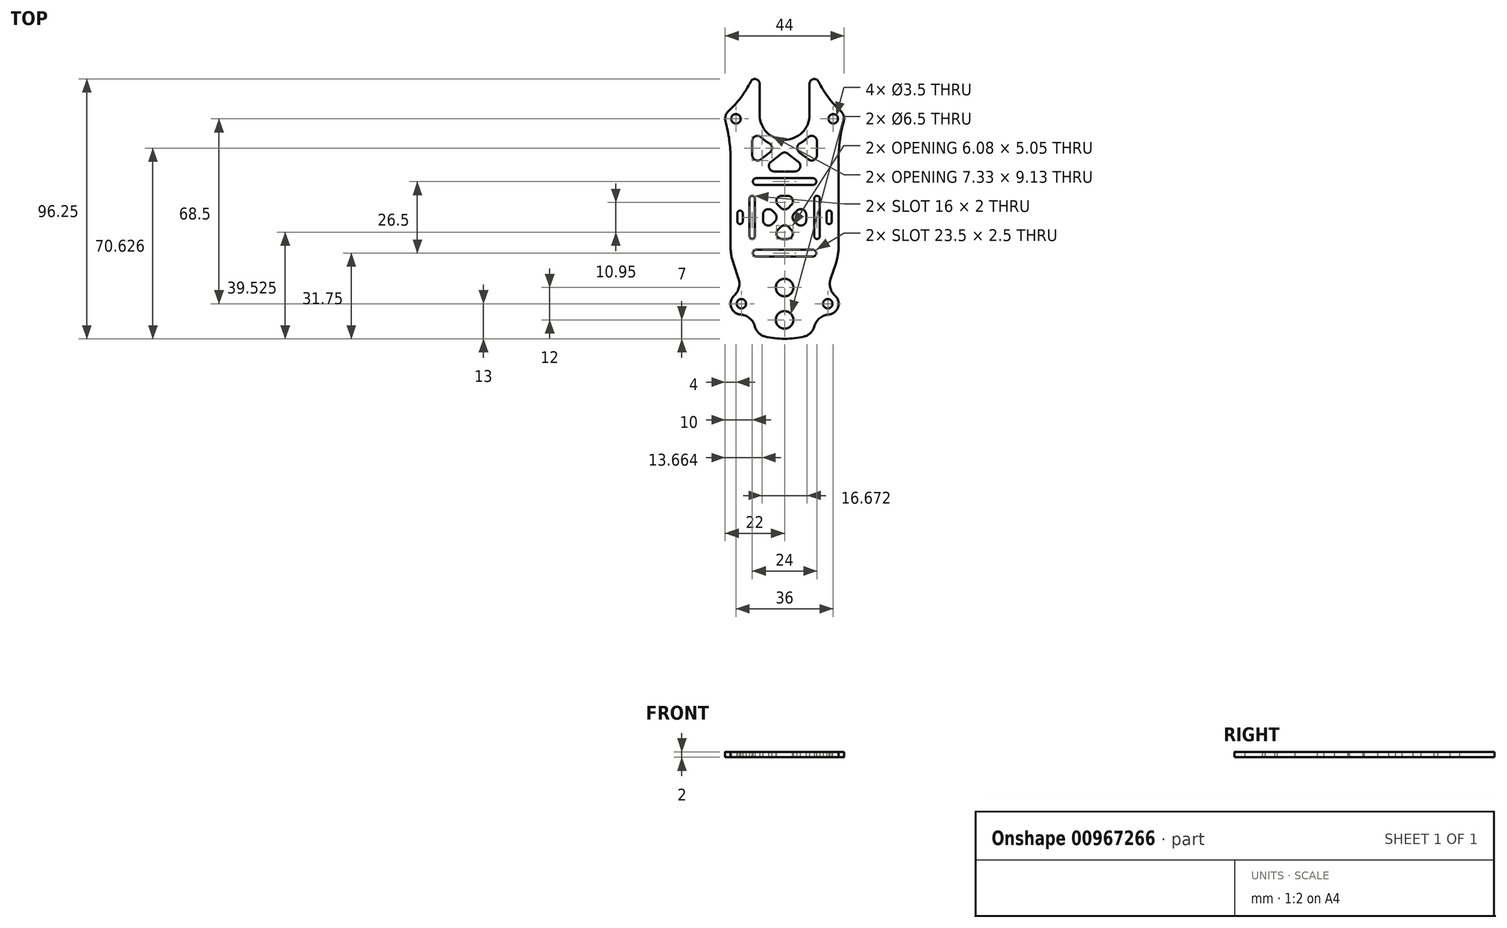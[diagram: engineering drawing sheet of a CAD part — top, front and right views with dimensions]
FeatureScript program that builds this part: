
annotation { "Feature Type Name" : "Feature", "Feature Type Description" : "" }
export const myFeature = defineFeature(function(context is Context, id is Id, definition is map)
    precondition{}
    {
        {
            var Q0;
            Q0=qCreatedBy(makeId("Top.planeOp"),FACE);
            var sketch = newSketch(context, id + "F0", { "sketchPlane" : qUnion([Q0])});
            skArc(sketch, "E0", {"start": v(-20.7, 39.46) * mm, "mid": v(-21.84, 37.62) * mm, "end": v(-21.86, 35.44) * mm});
            skLineSegment(sketch, "E1", {"start": v(-18.93, -17.14) * mm, "end": v(-17.05, -22.66) * mm});
            skLineSegment(sketch, "E2", {"start": v(0, 24) * mm, "end": v(0, -60) * mm, "construction": true});
            skCircle(sketch, "E3", {"center": v(-16, -32) * mm, "radius": 1.75 * mm});
            skArc(sketch, "E4.MirrorCS", {"start": v(20.7, 39.46) * mm, "mid": v(21.84, 37.62) * mm, "end": v(21.86, 35.44) * mm});
            skCircle(sketch, "E5.MirrorC", {"center": v(16, -32) * mm, "radius": 1.75 * mm});
            skLineSegment(sketch, "E6.MirrorCS", {"start": v(18.93, -17.14) * mm, "end": v(17.05, -22.66) * mm});
            skCircle(sketch, "E7", {"center": v(-18, 36.5) * mm, "radius": 1.75 * mm});
            skCircle(sketch, "E8.MirrorC", {"center": v(18, 36.5) * mm, "radius": 1.75 * mm});
            skCircle(sketch, "E9", {"center": v(0, -38) * mm, "radius": 3.25 * mm});
            skArc(sketch, "E10", {"start": v(-7.28, -44.13) * mm, "mid": v(-3.66, -44.78) * mm, "end": v(0, -45) * mm});
            skLineSegment(sketch, "E11.trimOffspring", {"start": v(-20, 21.67) * mm, "end": v(-20, -10.69) * mm});
            skArc(sketch, "E12", {"start": v(16.32, -35.99) * mm, "mid": v(19.79, -33.3) * mm, "end": v(18.7, -29.04) * mm});
            skArc(sketch, "E13.filletArc", {"start": v(16.32, -35.99) * mm, "mid": v(13.12, -37.23) * mm, "end": v(11.13, -40.03) * mm});
            skArc(sketch, "E14.filletArc", {"start": v(17.05, -22.66) * mm, "mid": v(16.92, -26.1) * mm, "end": v(18.7, -29.04) * mm});
            skArc(sketch, "E15.MirrorCS", {"start": v(-16.32, -35.99) * mm, "mid": v(-13.12, -37.23) * mm, "end": v(-11.13, -40.03) * mm});
            skArc(sketch, "E16.MirrorCS", {"start": v(-16.32, -35.99) * mm, "mid": v(-19.79, -33.3) * mm, "end": v(-18.7, -29.04) * mm});
            skArc(sketch, "E17.MirrorCS", {"start": v(-17.05, -22.66) * mm, "mid": v(-16.92, -26.1) * mm, "end": v(-18.7, -29.04) * mm});
            skLineSegment(sketch, "E18", {"start": v(-11.13, -40.03) * mm, "end": v(-10.84, -40.89) * mm});
            skLineSegment(sketch, "E19", {"start": v(11.13, -40.03) * mm, "end": v(10.84, -40.89) * mm});
            skLineSegment(sketch, "E20", {"start": v(-17.05, -22.66) * mm, "end": v(-11.13, -40.03) * mm, "construction": true});
            skLineSegment(sketch, "E21", {"start": v(17.05, -22.66) * mm, "end": v(11.13, -40.03) * mm, "construction": true});
            skArc(sketch, "E22", {"start": v(-9.25, 49.5) * mm, "mid": v(-10.6, 51.2) * mm, "end": v(-12.57, 50.27) * mm});
            skArc(sketch, "E23", {"start": v(-20.7, 39.46) * mm, "mid": v(-16.12, 44.48) * mm, "end": v(-12.57, 50.27) * mm});
            skArc(sketch, "E24.MirrorCS", {"start": v(9.25, 49.5) * mm, "mid": v(10.6, 51.2) * mm, "end": v(12.57, 50.27) * mm});
            skArc(sketch, "E25.MirrorCS", {"start": v(20.7, 39.46) * mm, "mid": v(16.12, 44.48) * mm, "end": v(12.57, 50.27) * mm});
            skPoint(sketch, "E26.visualSharp", {"position": v(-10, -43.34) * mm});
            skArc(sketch, "E26.filletArc", {"start": v(-10.84, -40.89) * mm, "mid": v(-9.47, -42.97) * mm, "end": v(-7.28, -44.13) * mm});
            skPoint(sketch, "E27.visualSharp", {"position": v(10, -43.34) * mm});
            skArc(sketch, "E27.filletArc", {"start": v(7.28, -44.13) * mm, "mid": v(9.47, -42.97) * mm, "end": v(10.84, -40.89) * mm});
            skLineSegment(sketch, "E28", {"start": v(-16.5, 1.5) * mm, "end": v(-16.5, -1.5) * mm, "construction": true});
            skArc(sketch, "E29.0.startCap", {"start": v(-17.5, 1.5) * mm, "mid": v(-16.5, 2.5) * mm, "end": v(-15.5, 1.5) * mm});
            skArc(sketch, "E29.0.endCap", {"start": v(-15.5, -1.5) * mm, "mid": v(-16.5, -2.5) * mm, "end": v(-17.5, -1.5) * mm});
            skLineSegment(sketch, "E29.0.left", {"start": v(-15.5, 1.5) * mm, "end": v(-15.5, -1.5) * mm});
            skLineSegment(sketch, "E29.0.right", {"start": v(-17.5, 1.5) * mm, "end": v(-17.5, -1.5) * mm});
            skLineSegment(sketch, "E30.MirrorCS", {"start": v(16.5, 1.5) * mm, "end": v(16.5, -1.5) * mm, "construction": true});
            skLineSegment(sketch, "E31.MirrorCS", {"start": v(15.5, 1.5) * mm, "end": v(15.5, -1.5) * mm});
            skLineSegment(sketch, "E32.MirrorCS", {"start": v(17.5, 1.5) * mm, "end": v(17.5, -1.5) * mm});
            skArc(sketch, "E33.MirrorCS", {"start": v(17.5, 1.5) * mm, "mid": v(16.5, 2.5) * mm, "end": v(15.5, 1.5) * mm});
            skArc(sketch, "E34.MirrorCS", {"start": v(15.5, -1.5) * mm, "mid": v(16.5, -2.5) * mm, "end": v(17.5, -1.5) * mm});
            skArc(sketch, "E35", {"start": v(-20, 21.67) * mm, "mid": v(-20.47, 28.62) * mm, "end": v(-21.86, 35.44) * mm});
            skArc(sketch, "E36.MirrorCS", {"start": v(20, 21.67) * mm, "mid": v(20.47, 28.62) * mm, "end": v(21.86, 35.44) * mm});
            skCircle(sketch, "E37", {"center": v(0, -38) * mm, "radius": 4.5 * mm, "construction": true});
            skLineSegment(sketch, "E38", {"start": v(20, 21.67) * mm, "end": v(20, -10.69) * mm});
            skLineSegment(sketch, "E39", {"start": v(-10.5, 13.25) * mm, "end": v(10.5, 13.25) * mm, "construction": true});
            skLineSegment(sketch, "E40", {"start": v(-10.5, -13.25) * mm, "end": v(10.5, -13.25) * mm, "construction": true});
            skArc(sketch, "E41.0.startCap", {"start": v(-10.5, 12) * mm, "mid": v(-11.75, 13.25) * mm, "end": v(-10.5, 14.5) * mm});
            skArc(sketch, "E41.0.endCap", {"start": v(10.5, 14.5) * mm, "mid": v(11.75, 13.25) * mm, "end": v(10.5, 12) * mm});
            skLineSegment(sketch, "E41.0.left", {"start": v(-10.5, 14.5) * mm, "end": v(10.5, 14.5) * mm});
            skLineSegment(sketch, "E41.0.right", {"start": v(-10.5, 12) * mm, "end": v(10.5, 12) * mm});
            skArc(sketch, "E41.1.startCap", {"start": v(-10.5, -14.5) * mm, "mid": v(-11.75, -13.25) * mm, "end": v(-10.5, -12) * mm});
            skArc(sketch, "E41.1.endCap", {"start": v(10.5, -12) * mm, "mid": v(11.75, -13.25) * mm, "end": v(10.5, -14.5) * mm});
            skLineSegment(sketch, "E41.1.left", {"start": v(-10.5, -12) * mm, "end": v(10.5, -12) * mm});
            skLineSegment(sketch, "E41.1.right", {"start": v(-10.5, -14.5) * mm, "end": v(10.5, -14.5) * mm});
            skPoint(sketch, "E42.visualSharp", {"position": v(-20, -14) * mm});
            skArc(sketch, "E42.filletArc", {"start": v(-20, -10.69) * mm, "mid": v(-19.73, -13.96) * mm, "end": v(-18.93, -17.14) * mm});
            skPoint(sketch, "E43.visualSharp", {"position": v(20, -14) * mm});
            skArc(sketch, "E43.filletArc", {"start": v(18.93, -17.14) * mm, "mid": v(19.73, -13.96) * mm, "end": v(20, -10.69) * mm});
            skLineSegment(sketch, "E44", {"start": v(-12, 7) * mm, "end": v(-12, -7) * mm, "construction": true});
            skLineSegment(sketch, "E45.MirrorCS", {"start": v(12, 7) * mm, "end": v(12, -7) * mm, "construction": true});
            skArc(sketch, "E46.0.startCap", {"start": v(-13, 7) * mm, "mid": v(-12, 8) * mm, "end": v(-11, 7) * mm});
            skArc(sketch, "E46.0.endCap", {"start": v(-11, -7) * mm, "mid": v(-12, -8) * mm, "end": v(-13, -7) * mm});
            skLineSegment(sketch, "E46.0.left", {"start": v(-11, 7) * mm, "end": v(-11, -7) * mm});
            skLineSegment(sketch, "E46.0.right", {"start": v(-13, 7) * mm, "end": v(-13, -7) * mm});
            skArc(sketch, "E46.3.startCap", {"start": v(11, 7) * mm, "mid": v(12, 8) * mm, "end": v(13, 7) * mm});
            skArc(sketch, "E46.3.endCap", {"start": v(13, -7) * mm, "mid": v(12, -8) * mm, "end": v(11, -7) * mm});
            skLineSegment(sketch, "E46.3.left", {"start": v(13, 7) * mm, "end": v(13, -7) * mm});
            skLineSegment(sketch, "E46.3.right", {"start": v(11, 7) * mm, "end": v(11, -7) * mm});
            skPoint(sketch, "E47.startSnap0", {"position": v(-16.5, 2.5) * mm});
            skArc(sketch, "E48.trimOffspring", {"start": v(0, -45) * mm, "mid": v(3.66, -44.78) * mm, "end": v(7.28, -44.13) * mm});
            skCircle(sketch, "E49", {"center": v(0, -26) * mm, "radius": 3.25 * mm});
            skLineSegment(sketch, "E50", {"start": v(-9.25, 49.5) * mm, "end": v(-9.25, 38) * mm});
            skLineSegment(sketch, "E51.MirrorCS", {"start": v(9.25, 49.5) * mm, "end": v(9.25, 38) * mm});
            skArc(sketch, "E52", {"start": v(-9.25, 38) * mm, "mid": v(0, 28.75) * mm, "end": v(9.25, 38) * mm});
            skSolve(sketch);
        }
        {
            var Q0;
            Q0=qSketchRegion(id+"F0",true);
            var Q1;
            Q1=makeQuery(id+"F0.imprint","IMPRINT",FACE,{"disambiguationData":[TD([[makeQuery(id+"F0.imprint","IMPRINT",EDGE,{"derivedFrom":sQuery(id+"F0.wireOp",EDGE,"f439a884-37bc-483a-9020-57d0572b4fa8.sketch_text.stroke-0")}),-1.0]])]});
            var Q2;
            Q2=makeQuery(id+"F0.imprint","IMPRINT",FACE,{"disambiguationData":[TD([[makeQuery(id+"F0.imprint","IMPRINT",EDGE,{"derivedFrom":sQuery(id+"F0.wireOp",EDGE,"f439a884-37bc-483a-9020-57d0572b4fa8.sketch_text.stroke-27")}),-1.0]])]});
            extrude(context, id + "F1", {"entities" : qUnion([Q0, Q1, Q2]), "depth" : 2 * mm});
        }
        {
            var Q0;
            Q0=makeQuery(id+"F1.opExtrude","CAP_FACE",FACE,{"disambiguationData":[OSD([sQuery(id+"F0.wireOp",EDGE,"E0"),sQuery(id+"F0.wireOp",EDGE,"E1"),sQuery(id+"F0.wireOp",EDGE,"E3"),sQuery(id+"F0.wireOp",EDGE,"E4.MirrorCS"),sQuery(id+"F0.wireOp",EDGE,"E5.MirrorC"),sQuery(id+"F0.wireOp",EDGE,"E6.MirrorCS"),sQuery(id+"F0.wireOp",EDGE,"E7"),sQuery(id+"F0.wireOp",EDGE,"E8.MirrorC"),sQuery(id+"F0.wireOp",EDGE,"E9"),sQuery(id+"F0.wireOp",EDGE,"E10"),sQuery(id+"F0.wireOp",EDGE,"E11.trimOffspring"),sQuery(id+"F0.wireOp",EDGE,"E12"),sQuery(id+"F0.wireOp",EDGE,"E13.filletArc"),sQuery(id+"F0.wireOp",EDGE,"E14.filletArc"),sQuery(id+"F0.wireOp",EDGE,"E15.MirrorCS"),sQuery(id+"F0.wireOp",EDGE,"E16.MirrorCS"),sQuery(id+"F0.wireOp",EDGE,"E17.MirrorCS"),sQuery(id+"F0.wireOp",EDGE,"E18"),sQuery(id+"F0.wireOp",EDGE,"E19"),sQuery(id+"F0.wireOp",EDGE,"E22"),sQuery(id+"F0.wireOp",EDGE,"E23"),sQuery(id+"F0.wireOp",EDGE,"E24.MirrorCS"),sQuery(id+"F0.wireOp",EDGE,"E25.MirrorCS"),sQuery(id+"F0.wireOp",EDGE,"E26.filletArc"),sQuery(id+"F0.wireOp",EDGE,"E27.filletArc"),sQuery(id+"F0.wireOp",EDGE,"E29.0.startCap"),sQuery(id+"F0.wireOp",EDGE,"E29.0.endCap"),sQuery(id+"F0.wireOp",EDGE,"E29.0.left"),sQuery(id+"F0.wireOp",EDGE,"E29.0.right"),sQuery(id+"F0.wireOp",EDGE,"E31.MirrorCS"),sQuery(id+"F0.wireOp",EDGE,"E32.MirrorCS"),sQuery(id+"F0.wireOp",EDGE,"E33.MirrorCS"),sQuery(id+"F0.wireOp",EDGE,"E34.MirrorCS"),sQuery(id+"F0.wireOp",EDGE,"E35"),sQuery(id+"F0.wireOp",EDGE,"E36.MirrorCS"),sQuery(id+"F0.wireOp",EDGE,"E38"),sQuery(id+"F0.wireOp",EDGE,"E41.0.startCap"),sQuery(id+"F0.wireOp",EDGE,"E41.0.endCap"),sQuery(id+"F0.wireOp",EDGE,"E41.0.left"),sQuery(id+"F0.wireOp",EDGE,"E41.0.right"),sQuery(id+"F0.wireOp",EDGE,"E41.1.startCap"),sQuery(id+"F0.wireOp",EDGE,"E41.1.endCap"),sQuery(id+"F0.wireOp",EDGE,"E41.1.left"),sQuery(id+"F0.wireOp",EDGE,"E41.1.right"),sQuery(id+"F0.wireOp",EDGE,"E42.filletArc"),sQuery(id+"F0.wireOp",EDGE,"E43.filletArc"),sQuery(id+"F0.wireOp",EDGE,"E46.0.startCap"),sQuery(id+"F0.wireOp",EDGE,"E46.0.endCap"),sQuery(id+"F0.wireOp",EDGE,"E46.0.left"),sQuery(id+"F0.wireOp",EDGE,"E46.0.right"),sQuery(id+"F0.wireOp",EDGE,"E46.3.startCap"),sQuery(id+"F0.wireOp",EDGE,"E46.3.endCap"),sQuery(id+"F0.wireOp",EDGE,"E46.3.left"),sQuery(id+"F0.wireOp",EDGE,"E46.3.right"),sQuery(id+"F0.wireOp",EDGE,"E48.trimOffspring"),sQuery(id+"F0.wireOp",EDGE,"E49"),sQuery(id+"F0.wireOp",EDGE,"E50"),sQuery(id+"F0.wireOp",EDGE,"E51.MirrorCS"),sQuery(id+"F0.wireOp",EDGE,"E52")])],"isStart":false});
            var sketch = newSketch(context, id + "F2", { "sketchPlane" : qUnion([Q0])});
            skLineSegment(sketch, "E53.bottom", {"start": v(-1.05, 8) * mm, "end": v(1.05, 8) * mm});
            skLineSegment(sketch, "E53.top", {"start": v(-1.05, -8) * mm, "end": v(1.05, -8) * mm});
            skLineSegment(sketch, "E53.left", {"start": v(-8, 1.05) * mm, "end": v(-8, -1.05) * mm});
            skLineSegment(sketch, "E53.right", {"start": v(8, 1.05) * mm, "end": v(8, -1.05) * mm});
            skLineSegment(sketch, "E54.bottom", {"start": v(-12, 36) * mm, "end": v(12, 36) * mm, "construction": true});
            skLineSegment(sketch, "E54.top", {"start": v(-3.83, 17) * mm, "end": v(3.83, 17) * mm});
            skLineSegment(sketch, "E54.left", {"start": v(-12, 28.2) * mm, "end": v(-12, 23.05) * mm});
            skLineSegment(sketch, "E54.right", {"start": v(12, 28.2) * mm, "end": v(12, 23.05) * mm});
            skArc(sketch, "E55", {"start": v(-8.57, 29.6) * mm, "mid": v(-7.22, 28.42) * mm, "end": v(-5.71, 27.45) * mm});
            skPoint(sketch, "E55.centerSnap0", {"position": v(0, 36) * mm});
            skLineSegment(sketch, "E56", {"start": v(-8, 8) * mm, "end": v(8, -8) * mm, "construction": true});
            skLineSegment(sketch, "E57", {"start": v(-8, -8) * mm, "end": v(8, 8) * mm, "construction": true});
            skLineSegment(sketch, "E58", {"start": v(-12, 36) * mm, "end": v(12, 17) * mm, "construction": true});
            skLineSegment(sketch, "E59", {"start": v(-12, 17) * mm, "end": v(12, 36) * mm, "construction": true});
            skLineSegment(sketch, "E60", {"start": v(1.24, 23.6) * mm, "end": v(5.08, 20.57) * mm});
            skLineSegment(sketch, "E61", {"start": v(5.42, 24.12) * mm, "end": v(8.76, 21.48) * mm});
            skLineSegment(sketch, "E62.MirrorCS", {"start": v(-5.42, 24.12) * mm, "end": v(-8.76, 21.48) * mm});
            skLineSegment(sketch, "E63.MirrorCS", {"start": v(-1.24, 23.6) * mm, "end": v(-5.08, 20.57) * mm});
            skArc(sketch, "E64.trimOffspring", {"start": v(5.71, 27.45) * mm, "mid": v(7.22, 28.42) * mm, "end": v(8.57, 29.6) * mm});
            skPoint(sketch, "E65.orphan", {"position": v(2, 26.17) * mm});
            skPoint(sketch, "E66.orphan", {"position": v(-2, 26.17) * mm});
            skLineSegment(sketch, "E67", {"start": v(-12, 38) * mm, "end": v(-12, 36) * mm, "construction": true});
            skLineSegment(sketch, "E68", {"start": v(12, 38) * mm, "end": v(12, 36) * mm, "construction": true});
            skPoint(sketch, "E69.visualSharp", {"position": v(-12, 38) * mm});
            skArc(sketch, "E69.filletArc", {"start": v(-8.57, 29.6) * mm, "mid": v(-10.76, 30.05) * mm, "end": v(-12, 28.2) * mm});
            skPoint(sketch, "E70.visualSharp", {"position": v(-2.67, 26.3) * mm});
            skArc(sketch, "E70.filletArc", {"start": v(-5.42, 24.12) * mm, "mid": v(-4.67, 25.86) * mm, "end": v(-5.71, 27.45) * mm});
            skPoint(sketch, "E71.visualSharp", {"position": v(-12, 18.91) * mm});
            skArc(sketch, "E71.filletArc", {"start": v(-12, 23.05) * mm, "mid": v(-10.87, 21.25) * mm, "end": v(-8.76, 21.48) * mm});
            skPoint(sketch, "E72.visualSharp", {"position": v(-9.58, 17) * mm});
            skArc(sketch, "E72.filletArc", {"start": v(-5.08, 20.57) * mm, "mid": v(-5.72, 18.34) * mm, "end": v(-3.83, 17) * mm});
            skPoint(sketch, "E73.visualSharp", {"position": v(9.58, 17) * mm});
            skArc(sketch, "E73.filletArc", {"start": v(3.83, 17) * mm, "mid": v(5.72, 18.34) * mm, "end": v(5.08, 20.57) * mm});
            skPoint(sketch, "E74.visualSharp", {"position": v(0, 24.59) * mm});
            skArc(sketch, "E74.filletArc", {"start": v(1.24, 23.6) * mm, "mid": v(0, 24.04) * mm, "end": v(-1.24, 23.6) * mm});
            skPoint(sketch, "E75.visualSharp", {"position": v(2.67, 26.3) * mm});
            skArc(sketch, "E75.filletArc", {"start": v(5.71, 27.45) * mm, "mid": v(4.67, 25.86) * mm, "end": v(5.42, 24.12) * mm});
            skPoint(sketch, "E76.visualSharp", {"position": v(12, 18.91) * mm});
            skArc(sketch, "E76.filletArc", {"start": v(8.76, 21.48) * mm, "mid": v(10.87, 21.25) * mm, "end": v(12, 23.05) * mm});
            skPoint(sketch, "E77.visualSharp", {"position": v(12, 38) * mm});
            skArc(sketch, "E77.filletArc", {"start": v(12, 28.2) * mm, "mid": v(10.76, 30.05) * mm, "end": v(8.57, 29.6) * mm});
            skLineSegment(sketch, "E78", {"start": v(-2.46, 4.59) * mm, "end": v(-1.41, 3.54) * mm});
            skLineSegment(sketch, "E79", {"start": v(-4.59, 2.46) * mm, "end": v(-3.54, 1.41) * mm});
            skLineSegment(sketch, "E80.MirrorCS", {"start": v(2.46, 4.59) * mm, "end": v(1.41, 3.54) * mm});
            skLineSegment(sketch, "E81.MirrorCS", {"start": v(4.59, 2.46) * mm, "end": v(3.54, 1.41) * mm});
            skLineSegment(sketch, "E82.trimOffspring", {"start": v(-3.54, -1.41) * mm, "end": v(-4.59, -2.46) * mm});
            skLineSegment(sketch, "E83.trimOffspring", {"start": v(1.41, -3.54) * mm, "end": v(2.46, -4.59) * mm});
            skLineSegment(sketch, "E84.trimOffspring", {"start": v(-1.41, -3.54) * mm, "end": v(-2.46, -4.59) * mm});
            skLineSegment(sketch, "E85.trimOffspring", {"start": v(3.54, -1.41) * mm, "end": v(4.59, -2.46) * mm});
            skPoint(sketch, "E86.visualSharp", {"position": v(-5.88, 8) * mm});
            skArc(sketch, "E86.filletArc", {"start": v(-1.05, 8) * mm, "mid": v(-2.9, 6.77) * mm, "end": v(-2.46, 4.59) * mm});
            skPoint(sketch, "E87.visualSharp", {"position": v(5.88, 8) * mm});
            skArc(sketch, "E87.filletArc", {"start": v(2.46, 4.59) * mm, "mid": v(2.9, 6.77) * mm, "end": v(1.05, 8) * mm});
            skPoint(sketch, "E88.visualSharp", {"position": v(0, 2.12) * mm});
            skArc(sketch, "E88.filletArc", {"start": v(-1.41, 3.54) * mm, "mid": v(0, 2.95) * mm, "end": v(1.41, 3.54) * mm});
            skPoint(sketch, "E89.visualSharp", {"position": v(-8, 5.88) * mm});
            skArc(sketch, "E89.filletArc", {"start": v(-4.59, 2.46) * mm, "mid": v(-6.77, 2.9) * mm, "end": v(-8, 1.05) * mm});
            skPoint(sketch, "E90.visualSharp", {"position": v(-8, -5.88) * mm});
            skArc(sketch, "E90.filletArc", {"start": v(-8, -1.05) * mm, "mid": v(-6.77, -2.9) * mm, "end": v(-4.59, -2.46) * mm});
            skPoint(sketch, "E91.visualSharp", {"position": v(-5.88, -8) * mm});
            skArc(sketch, "E91.filletArc", {"start": v(-2.46, -4.59) * mm, "mid": v(-2.9, -6.77) * mm, "end": v(-1.05, -8) * mm});
            skPoint(sketch, "E92.visualSharp", {"position": v(-2.12, 0) * mm});
            skArc(sketch, "E92.filletArc", {"start": v(-3.54, -1.41) * mm, "mid": v(-2.95, 0) * mm, "end": v(-3.54, 1.41) * mm});
            skPoint(sketch, "E93.visualSharp", {"position": v(5.88, -8) * mm});
            skArc(sketch, "E93.filletArc", {"start": v(1.05, -8) * mm, "mid": v(2.9, -6.77) * mm, "end": v(2.46, -4.59) * mm});
            skPoint(sketch, "E94.visualSharp", {"position": v(0, -2.12) * mm});
            skArc(sketch, "E94.filletArc", {"start": v(1.41, -3.54) * mm, "mid": v(0, -2.95) * mm, "end": v(-1.41, -3.54) * mm});
            skPoint(sketch, "E95.visualSharp", {"position": v(2.12, 0) * mm});
            skArc(sketch, "E95.filletArc", {"start": v(3.54, 1.41) * mm, "mid": v(2.95, 0) * mm, "end": v(3.54, -1.41) * mm});
            skPoint(sketch, "E96.visualSharp", {"position": v(8, -5.88) * mm});
            skArc(sketch, "E96.filletArc", {"start": v(4.59, -2.46) * mm, "mid": v(6.77, -2.9) * mm, "end": v(8, -1.05) * mm});
            skPoint(sketch, "E97.visualSharp", {"position": v(8, 5.88) * mm});
            skArc(sketch, "E97.filletArc", {"start": v(8, 1.05) * mm, "mid": v(6.77, 2.9) * mm, "end": v(4.59, 2.46) * mm});
            skSolve(sketch);
        }
        {
            var Q0;
            Q0=qSketchRegion(id+"F2",true);
            extrude(context, id + "F3", {"entities" : qUnion([Q0]), "operationType" : NewBodyOperationType.REMOVE, "oppositeDirection" : true, "depth" : 25 * mm});
        }
    });
